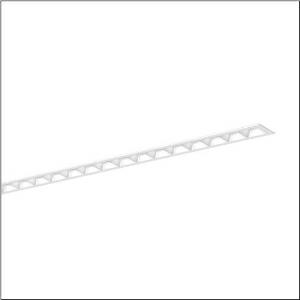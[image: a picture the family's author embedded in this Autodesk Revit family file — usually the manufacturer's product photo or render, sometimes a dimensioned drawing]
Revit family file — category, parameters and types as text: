
# Revit family: silica_r__21_51mx16dc3awb_c0f3
name_source: partatom
category: Lighting Fixtures
units: mm (PartAtom-declared; Revit-internal decimal feet)

## family parameters
Cut with Voids When Loaded = No
Host = Face
Light Source = No
Part Type = Normal
Room Calculation Point = No
Round Connector Dimension = Use Diameter
Shared = No

## types (1)
- --- (1 x LED, 10800 lm, 63.6 W, 3000K)
    Apparent Load = 64 VA
    CIE Flux Codes = 83 98 100 100 100
    Color Rendering = 80
    Color Temperature = 3000K
    Default Elevation = 1800 mm
    Description = Silica® 21, office luminaire, primary light control with darklight reflector, of PMMA, white, CAT 2 (L<= 3000cd/m²), light emission: direct distribution, primary light characteristic: symmetric, installation type: recessed, LED, rated luminous flux: 10.800lm, luminous efficacy: 170lm/W, light colour: 830, colour temperature: 3000K, control gear: DALI 2, with terminal, 3+2-pole, max. 2.5mm², mains connection: 220..240V, AC, 50/60Hz, rated input power: 63.6W, luminaire housing, of aluminium, traffic white (RAL 9016), length: 3.028mm, width: 79mm, height: 53mm, protection rating (complete): IP20, insulation class (complete): insulation class I (protective earthing), certification: CE, ENEC, VDE, permissible operating ambient temperature: 0..+35°C, standard: EN 50419, packaging unit: 1 piece
    Height = 0 mm  [stored 0 ft]
    Lamp = 1 x LED
    Lamp Light Flux = 10800 lm
    Lamp Power = 63.6 W
    Lamp count = 1
    Length = 3027 mm
    Luminous efficacy = 170 lm/W
    Manufacturer = Siteco
    ModVariant = No
    Model = 51MX16DC3AWB
    Mounting Place = Ceiling
    Mounting Type = Recessed
    Number of Poles = 1
    OnlyDefault = Yes
    Power Factor = 1
    Product Name = Silica® 21
    Product group = office luminaire | ceiling recessed
    ProductGroupID = 401
    Protection Class = Protection class I
    Protection Degree = IP 20
    RLX_Detail_Level = 1
    RLX_Emergency_Light_Flux = 0 lm
    RLX_Emergency_Type = 0
    RLX_Emergency_Type_DB = No
    RlxData = <blob elided: 60181 chars, md5=91d5c77c>
    Socket = socket
    Standby Power = 0 W
    System Light Flux = 10800 lm
    System Power = 64 W
    Type Comments = factory setting: luminous flux: 100 % | dim-lin: 254 | 360 mA
    Type Image = l_1335884.jpg
    URL = http://relux.com
    VarID = @adj_124000
    Voltage = 0 V
    Weight = 0.00 kg
    Width = 79 mm

note: [stored X ft] marks values corroborated as IEEE doubles in the binary element streams (Revit-internal decimal feet)

## geometry (parser evidence)
native form markers: Blend x4, Sweep x12
no freeform markers — native parametric forms only
